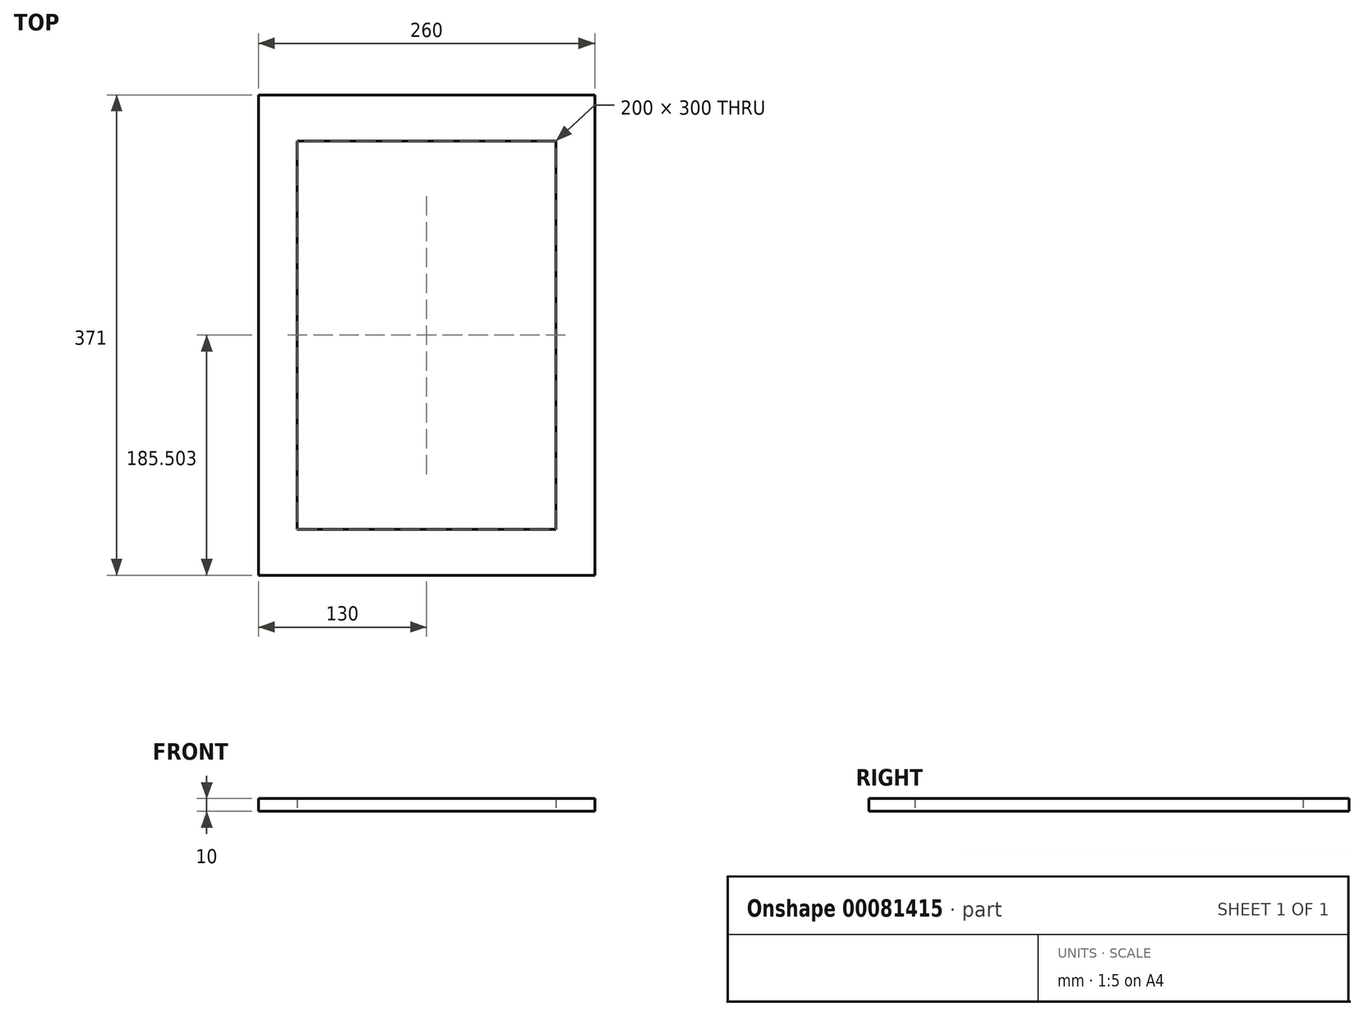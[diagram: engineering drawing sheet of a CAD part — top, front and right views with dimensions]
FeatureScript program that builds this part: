
annotation { "Feature Type Name" : "Feature", "Feature Type Description" : "" }
export const myFeature = defineFeature(function(context is Context, id is Id, definition is map)
    precondition{}
    {
        {
            var Q0;
            Q0=qCreatedBy(makeId("Top.planeOp"),FACE);
            var sketch = newSketch(context, id + "F0", { "sketchPlane" : qUnion([Q0])});
            skLineSegment(sketch, "E0.bottom", {"start": v(-125, -236.25) * mm, "end": v(135, -236.25) * mm});
            skLineSegment(sketch, "E0.top", {"start": v(-125, 134.75) * mm, "end": v(135, 134.75) * mm});
            skLineSegment(sketch, "E0.left", {"start": v(-125, -236.25) * mm, "end": v(-125, 134.75) * mm});
            skLineSegment(sketch, "E0.right", {"start": v(135, -236.25) * mm, "end": v(135, 134.75) * mm});
            skLineSegment(sketch, "E1.bottom", {"start": v(-95, 99.25) * mm, "end": v(105, 99.25) * mm});
            skLineSegment(sketch, "E1.top", {"start": v(-95, -200.75) * mm, "end": v(105, -200.75) * mm});
            skLineSegment(sketch, "E1.left", {"start": v(-95, 99.25) * mm, "end": v(-95, -200.75) * mm});
            skLineSegment(sketch, "E1.right", {"start": v(105, 99.25) * mm, "end": v(105, -200.75) * mm});
            skPoint(sketch, "E2.startSnap0", {"position": v(5, 99.25) * mm});
            skPoint(sketch, "E2.endSnap0", {"position": v(5, 99.25) * mm});
            skLineSegment(sketch, "E3", {"start": v(135, -50.75) * mm, "end": v(105, -50.75) * mm});
            skPoint(sketch, "E3.endSnap0", {"position": v(105, -50.75) * mm});
            skLineSegment(sketch, "E4", {"start": v(-125, -111.87) * mm, "end": v(-95, -111.87) * mm});
            skLineSegment(sketch, "E5", {"start": v(5.86, -236.25) * mm, "end": v(5.86, -200.75) * mm});
            skLineSegment(sketch, "E6", {"start": v(15.7, 99.25) * mm, "end": v(15.7, 134.75) * mm});
            skSolve(sketch);
        }
        {
            var Q0;
            Q0 = qSketchRegion(id + "F0", true);
            extrude(context, id + "F1", {"entities" : qUnion([Q0]), "depth" : 10 * mm});
        }
    });
